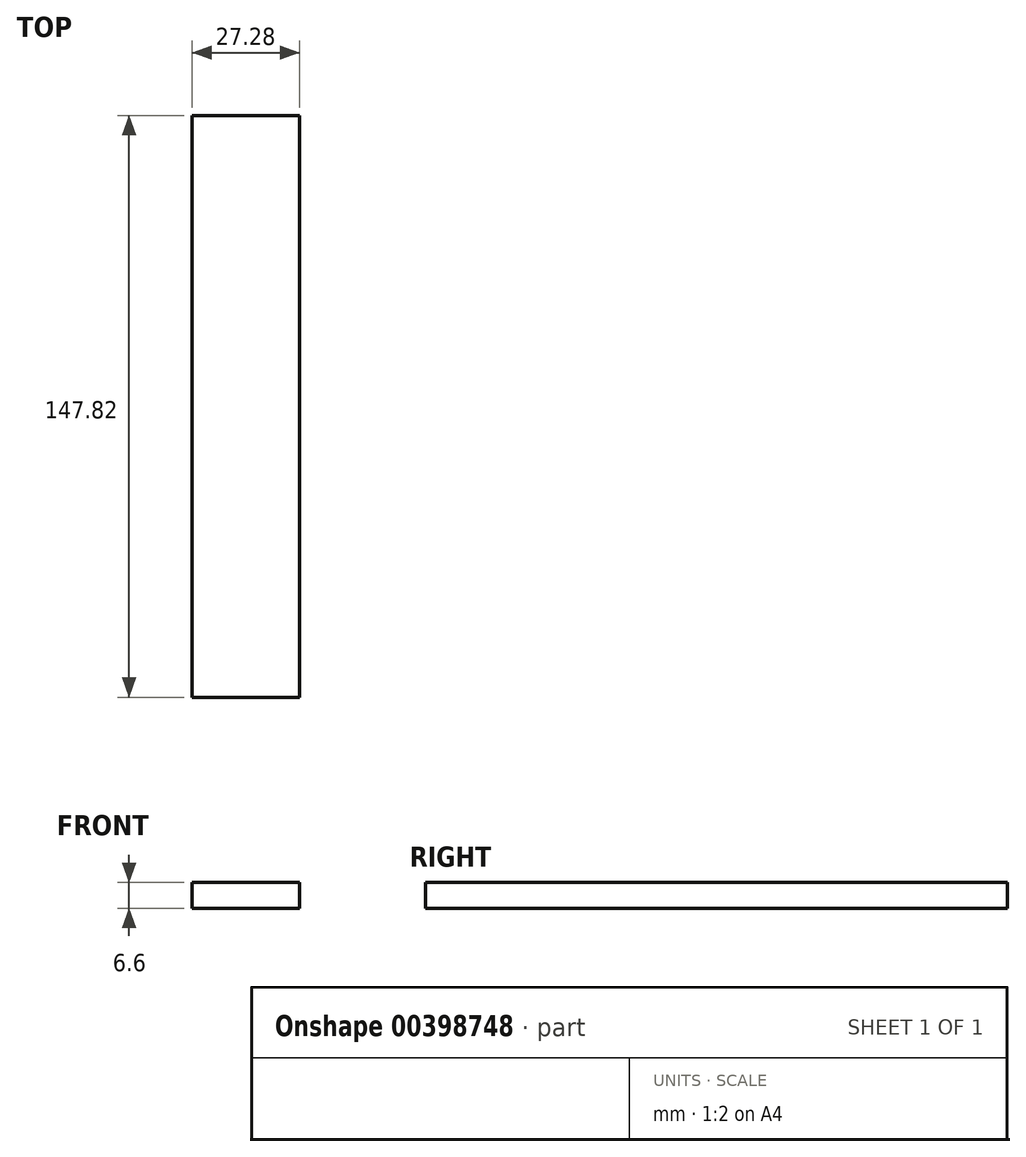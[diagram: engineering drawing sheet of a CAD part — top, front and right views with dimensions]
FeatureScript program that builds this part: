
annotation { "Feature Type Name" : "Feature", "Feature Type Description" : "" }
export const myFeature = defineFeature(function(context is Context, id is Id, definition is map)
    precondition{}
    {
        {
            var Q0;
            Q0=qCreatedBy(makeId("Top.planeOp"),FACE);
            var sketch = newSketch(context, id + "F0", { "sketchPlane" : qUnion([Q0])});
            skLineSegment(sketch, "E0.bottom", {"start": v(-13.64, -73.9) * mm, "end": v(13.64, -73.9) * mm});
            skLineSegment(sketch, "E0.top", {"start": v(-13.64, 73.9) * mm, "end": v(13.64, 73.9) * mm});
            skLineSegment(sketch, "E0.left", {"start": v(-13.64, -73.9) * mm, "end": v(-13.64, 73.9) * mm});
            skLineSegment(sketch, "E0.right", {"start": v(13.64, -73.9) * mm, "end": v(13.64, 73.9) * mm});
            skPoint(sketch, "E0.middle", {"position": v(0, 0) * mm});
            skSolve(sketch);
        }
        {
            var Q0;
            Q0=makeQuery(id+"F0.imprint","IMPRINT",FACE,{"disambiguationData":[TD([[makeQuery(id+"F0.imprint","IMPRINT",EDGE,{"derivedFrom":sQuery(id+"F0.wireOp",EDGE,"E0.bottom")}),1.0]])]});
            extrude(context, id + "F1", {"entities" : qUnion([Q0]), "depth" : 6.6 * mm});
        }
    });
